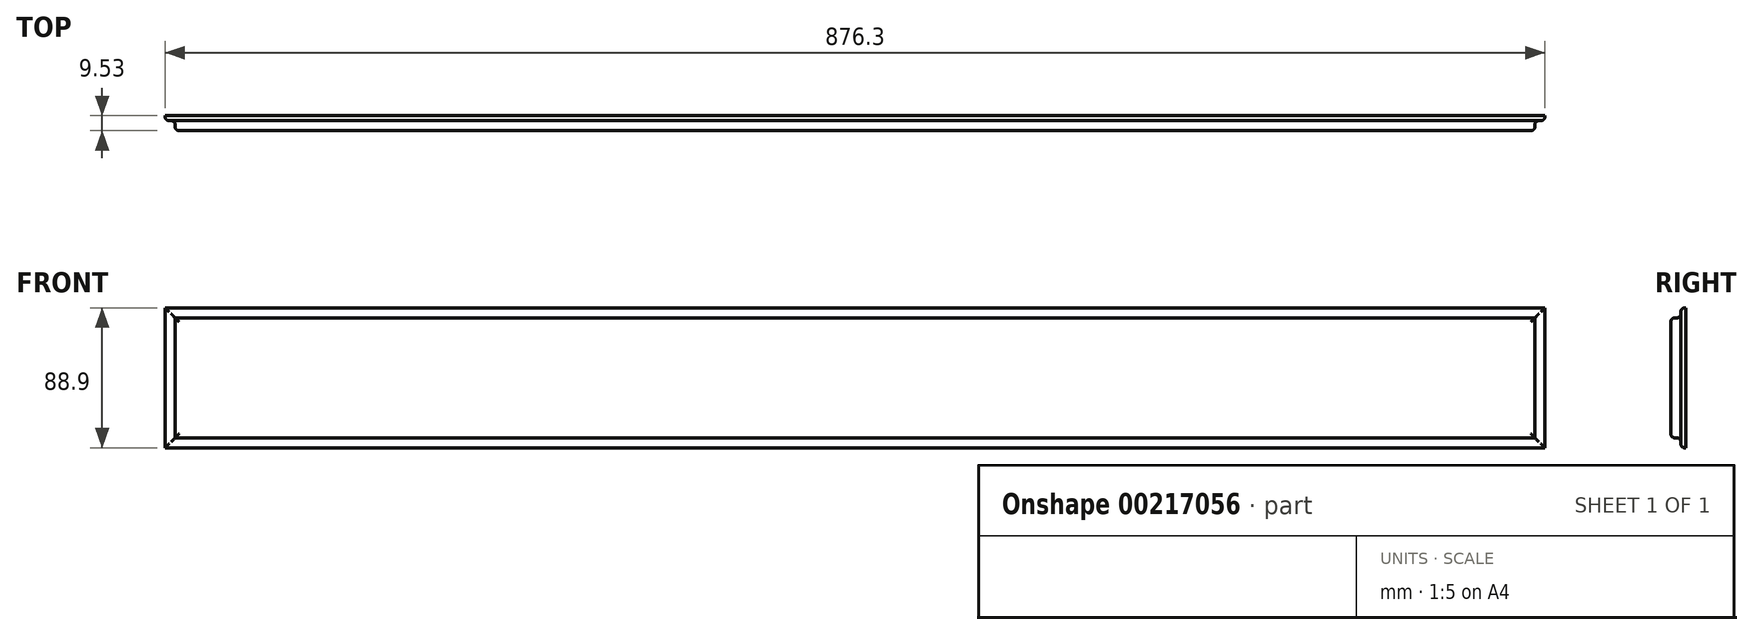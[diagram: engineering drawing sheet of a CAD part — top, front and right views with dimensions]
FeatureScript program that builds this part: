
annotation { "Feature Type Name" : "Feature", "Feature Type Description" : "" }
export const myFeature = defineFeature(function(context is Context, id is Id, definition is map)
    precondition{}
    {
        {
            var Q0;
            Q0=qCreatedBy(makeId("Front.planeOp"),FACE);
            var sketch = newSketch(context, id + "F0", { "sketchPlane" : qUnion([Q0])});
            skPoint(sketch, "E0.middle", {"position": v(0, 0) * mm});
            skLineSegment(sketch, "E1.0", {"start": v(-438.15, -44.45) * mm, "end": v(-438.15, 44.45) * mm});
            skLineSegment(sketch, "E1.1", {"start": v(438.15, -44.45) * mm, "end": v(-438.15, -44.45) * mm});
            skLineSegment(sketch, "E1.2", {"start": v(438.15, -44.45) * mm, "end": v(438.15, 44.45) * mm});
            skLineSegment(sketch, "E1.3", {"start": v(438.15, 44.45) * mm, "end": v(-438.15, 44.45) * mm});
            skPoint(sketch, "E0.right.end.orphan", {"position": v(-444.5, 50.8) * mm});
            skPoint(sketch, "E0.bottom.end.orphan", {"position": v(-444.5, -50.8) * mm});
            skPoint(sketch, "E0.left.end.orphan", {"position": v(444.5, 50.8) * mm});
            skPoint(sketch, "E0.left.start.orphan", {"position": v(444.5, -50.8) * mm});
            skLineSegment(sketch, "E2.0", {"start": v(431.8, 38.1) * mm, "end": v(-431.8, 38.1) * mm});
            skLineSegment(sketch, "E2.1", {"start": v(431.8, -38.1) * mm, "end": v(431.8, 38.1) * mm});
            skLineSegment(sketch, "E2.2", {"start": v(431.8, -38.1) * mm, "end": v(-431.8, -38.1) * mm});
            skLineSegment(sketch, "E2.3", {"start": v(-431.8, -38.1) * mm, "end": v(-431.8, 38.1) * mm});
            skSolve(sketch);
        }
        {
            var Q0;
            Q0=makeQuery(id+"F0.imprint","IMPRINT",FACE,{"disambiguationData":[TD([[makeQuery(id+"F0.imprint","IMPRINT",EDGE,{"derivedFrom":sQuery(id+"F0.wireOp",EDGE,"E2.0")}),1.0]])]});
            extrude(context, id + "F1", {"entities" : qUnion([Q0]), "depth" : 9.52 * mm});
        }
        {
            var Q0;
            Q0=makeQuery(id+"F0.imprint","IMPRINT",FACE,{"disambiguationData":[TD([[makeQuery(id+"F0.imprint","IMPRINT",EDGE,{"derivedFrom":sQuery(id+"F0.wireOp",EDGE,"E1.0")}),-1.0]])]});
            extrude(context, id + "F2", {"entities" : qUnion([Q0]), "operationType" : NewBodyOperationType.ADD, "depth" : 3.17 * mm});
        }
        {
            var Q0;
            Q0=makeQuery(id+"F1.opExtrude","CAP_FACE",FACE,{"disambiguationData":[OSD([sQuery(id+"F0.wireOp",EDGE,"E2.0"),sQuery(id+"F0.wireOp",EDGE,"E2.1"),sQuery(id+"F0.wireOp",EDGE,"E2.2"),sQuery(id+"F0.wireOp",EDGE,"E2.3")])],"isStart":false});
            var Q1;
            Q1=makeQuery(id+"F2.opExtrude","CAP_FACE",FACE,{"disambiguationData":[OSD([sQuery(id+"F0.wireOp",EDGE,"E1.0"),sQuery(id+"F0.wireOp",EDGE,"E1.1"),sQuery(id+"F0.wireOp",EDGE,"E1.2"),sQuery(id+"F0.wireOp",EDGE,"E1.3"),sQuery(id+"F0.wireOp",EDGE,"E2.0"),sQuery(id+"F0.wireOp",EDGE,"E2.1"),sQuery(id+"F0.wireOp",EDGE,"E2.2"),sQuery(id+"F0.wireOp",EDGE,"E2.3")])],"isStart":false});
            fillet(context, id + "F3", {"entities" : qUnion([Q0, Q1]), "radius" : 2.54 * mm, "tangentPropagation" : true, "allowEdgeOverflow" : false});
        }
    });
